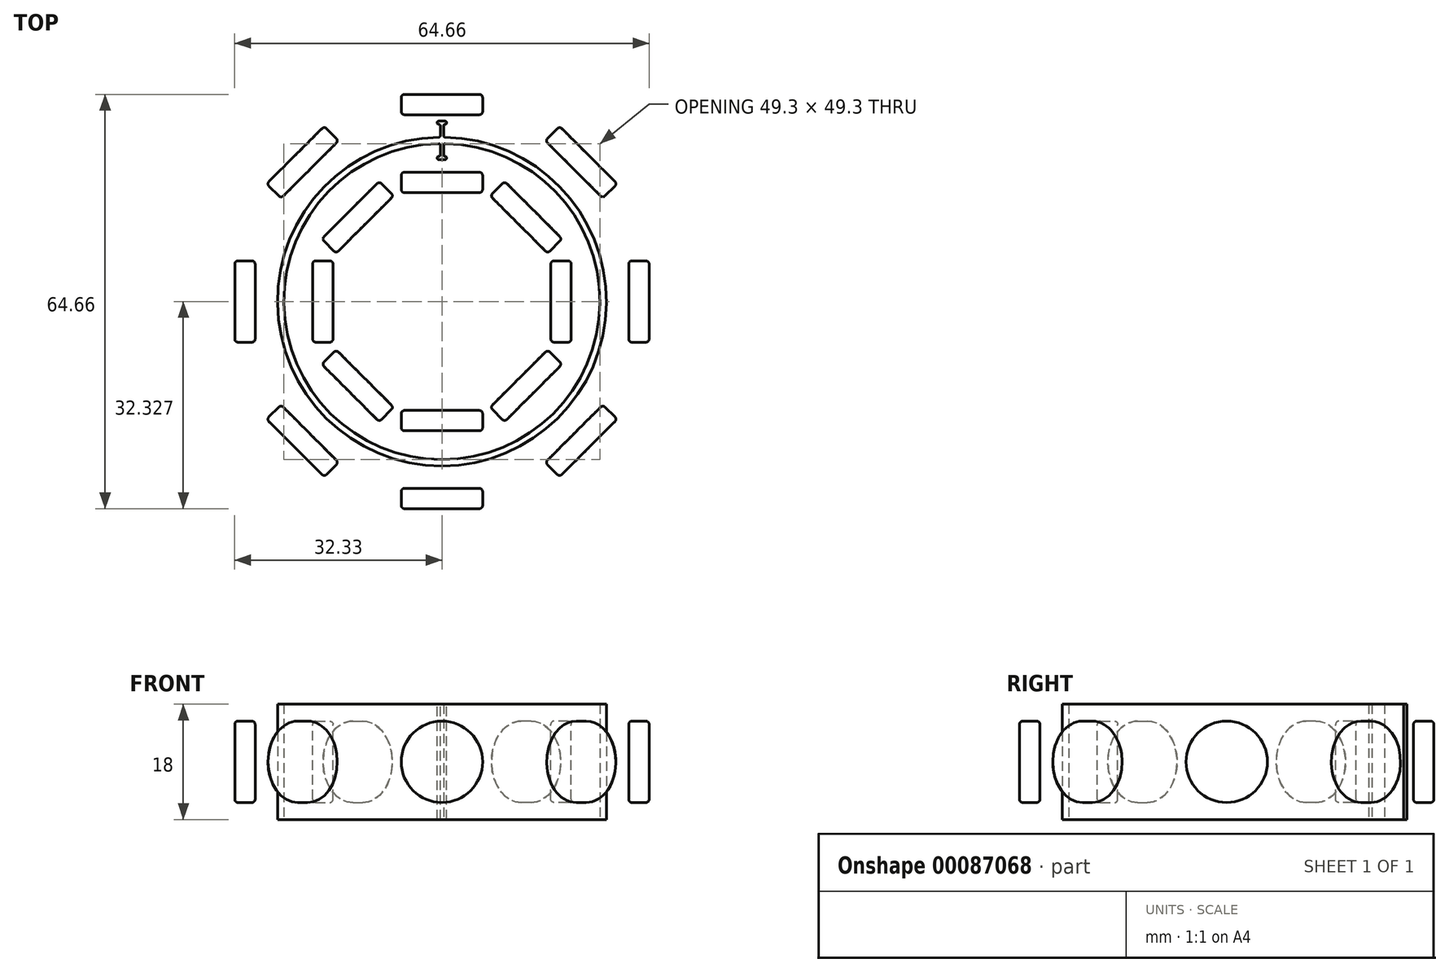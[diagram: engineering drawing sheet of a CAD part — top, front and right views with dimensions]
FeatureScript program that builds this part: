
annotation { "Feature Type Name" : "Feature", "Feature Type Description" : "" }
export const myFeature = defineFeature(function(context is Context, id is Id, definition is map)
    precondition{}
    {
        {
            var Q0;
            Q0=qCreatedBy(makeId("Top.planeOp"),FACE);
            var sketch = newSketch(context, id + "F0", { "sketchPlane" : qUnion([Q0])});
            skLineSegment(sketch, "E0", {"start": v(0, 0) * mm, "end": v(0, 17) * mm, "construction": true});
            skLineSegment(sketch, "E1.bottom", {"start": v(0, 17) * mm, "end": v(6.35, 17) * mm});
            skLineSegment(sketch, "E1.top", {"start": v(0, 20.17) * mm, "end": v(6.35, 20.17) * mm});
            skLineSegment(sketch, "E1.left", {"start": v(0, 17) * mm, "end": v(0, 20.17) * mm});
            skLineSegment(sketch, "E1.right", {"start": v(6.35, 17) * mm, "end": v(6.35, 20.17) * mm});
            skCircle(sketch, "E2", {"center": v(0, 0) * mm, "radius": 24.65 * mm});
            skCircle(sketch, "E3", {"center": v(0, 0) * mm, "radius": 25.65 * mm});
            skCircle(sketch, "E4", {"center": v(0, 0) * mm, "radius": 21.15 * mm, "construction": true});
            skLineSegment(sketch, "E5", {"start": v(0, 24.65) * mm, "end": v(0, 25.65) * mm, "construction": true});
            skLineSegment(sketch, "E6", {"start": v(0, 25.65) * mm, "end": v(0, 28.15) * mm, "construction": true});
            skLineSegment(sketch, "E7", {"start": v(0, 24.65) * mm, "end": v(0, 22.15) * mm, "construction": true});
            skCircle(sketch, "E8", {"center": v(0, 0) * mm, "radius": 29.15 * mm, "construction": true});
            skLineSegment(sketch, "E9", {"start": v(-29.15, 0) * mm, "end": v(-25.65, 0) * mm, "construction": true});
            skLineSegment(sketch, "E10", {"start": v(-25.65, 0) * mm, "end": v(-24.65, 0) * mm, "construction": true});
            skLineSegment(sketch, "E11", {"start": v(-24.65, 0) * mm, "end": v(-21.15, 0) * mm, "construction": true});
            skLineSegment(sketch, "E12.bottom", {"start": v(0, 29.15) * mm, "end": v(6.35, 29.15) * mm});
            skLineSegment(sketch, "E12.top", {"start": v(0, 32.33) * mm, "end": v(6.35, 32.33) * mm});
            skLineSegment(sketch, "E12.left", {"start": v(0, 29.15) * mm, "end": v(0, 32.33) * mm});
            skLineSegment(sketch, "E12.right", {"start": v(6.35, 29.15) * mm, "end": v(6.35, 32.33) * mm});
            skLineSegment(sketch, "E13.bottom", {"start": v(0.25, 28.15) * mm, "end": v(-0.25, 28.15) * mm});
            skLineSegment(sketch, "E13.top", {"start": v(0.25, 22.15) * mm, "end": v(-0.25, 22.15) * mm});
            skLineSegment(sketch, "E13.left", {"start": v(0.25, 28.15) * mm, "end": v(0.25, 22.15) * mm});
            skLineSegment(sketch, "E13.right", {"start": v(-0.25, 28.15) * mm, "end": v(-0.25, 22.15) * mm});
            skPoint(sketch, "E13.middle", {"position": v(0, 25.15) * mm});
            skLineSegment(sketch, "E14.bottom", {"start": v(-0.75, 22.65) * mm, "end": v(0.75, 22.65) * mm});
            skLineSegment(sketch, "E14.top", {"start": v(-0.75, 22.15) * mm, "end": v(0.75, 22.15) * mm});
            skLineSegment(sketch, "E14.left", {"start": v(-0.75, 22.65) * mm, "end": v(-0.75, 22.15) * mm});
            skLineSegment(sketch, "E14.right", {"start": v(0.75, 22.65) * mm, "end": v(0.75, 22.15) * mm});
            skLineSegment(sketch, "E15.bottom", {"start": v(-0.75, 27.65) * mm, "end": v(0.75, 27.65) * mm});
            skLineSegment(sketch, "E15.top", {"start": v(-0.75, 28.15) * mm, "end": v(0.75, 28.15) * mm});
            skLineSegment(sketch, "E15.left", {"start": v(-0.75, 27.65) * mm, "end": v(-0.75, 28.15) * mm});
            skLineSegment(sketch, "E15.right", {"start": v(0.75, 27.65) * mm, "end": v(0.75, 28.15) * mm});
            skSolve(sketch);
        }
        {
            var Q0;
            Q0=makeQuery(id+"F0.imprint","IMPRINT",FACE,{"disambiguationData":[TD([[makeQuery(id+"F0.imprint","IMPRINT",EDGE,{"derivedFrom":sQuery(id+"F0.wireOp",EDGE,"E12.bottom")}),1.0]])]});
            var Q1;
            Q1=makeQuery(id+"F0.imprint","IMPRINT",FACE,{"disambiguationData":[TD([[makeQuery(id+"F0.imprint","IMPRINT",EDGE,{"derivedFrom":sQuery(id+"F0.wireOp",EDGE,"E1.bottom")}),1.0]])]});
            var Q2;
            Q2=sQuery(id+"F0.wireOp",EDGE,"E0");
            revolve(context, id + "F1", {"entities" : qUnion([Q0, Q1]), "axis" : qUnion([Q2]), "revolveType" : RevolveType.FULL});
        }
        {
            var Q0;
            Q0=makeQuery(id+"F1.opRevolve","SWEPT_FACE",FACE,{"disambiguationData":[OSD([sQuery(id+"F0.wireOp",EDGE,"E1.top")])]});
            var Q1;
            Q1=makeQuery(id+"F1.opRevolve","SWEPT_FACE",FACE,{"disambiguationData":[OSD([sQuery(id+"F0.wireOp",EDGE,"E12.top")])]});
            var Q2;
            Q2=makeQuery(id+"F1.opRevolve","SWEPT_FACE",FACE,{"disambiguationData":[OSD([sQuery(id+"F0.wireOp",EDGE,"E12.bottom")])]});
            var Q3;
            Q3=makeQuery(id+"F1.opRevolve","SWEPT_FACE",FACE,{"disambiguationData":[OSD([sQuery(id+"F0.wireOp",EDGE,"E1.bottom")])]});
            fillet(context, id + "F2", {"entities" : qUnion([Q0, Q1, Q2, Q3]), "radius" : .5 * mm, "tangentPropagation" : true, "allowEdgeOverflow" : false});
        }
        {
            var Q0;
            Q0=makeQuery(id+"F1.opRevolve","SWEPT_BODY",BODY,{"disambiguationData":[OSD([sQuery(id+"F0.wireOp",EDGE,"E12.bottom"),sQuery(id+"F0.wireOp",EDGE,"E12.top"),sQuery(id+"F0.wireOp",EDGE,"E12.left"),sQuery(id+"F0.wireOp",EDGE,"E12.right")])]});
            var Q1;
            Q1=makeQuery(id+"F1.opRevolve","SWEPT_BODY",BODY,{"disambiguationData":[OSD([sQuery(id+"F0.wireOp",EDGE,"E1.bottom"),sQuery(id+"F0.wireOp",EDGE,"E1.top"),sQuery(id+"F0.wireOp",EDGE,"E1.left"),sQuery(id+"F0.wireOp",EDGE,"E1.right")])]});
            var Q2;
            Q2=sQuery(id+"F0.wireOp",EDGE,"E3");
            circularPattern(context, id + "F3", {"entities" : qUnion([Q0, Q1]), "axis" : qUnion([Q2]), "angle" : 360 * degree, "instanceCount" : 8, "equalSpace" : true});
        }
        {
            var Q0;
            {var subQ0=sQuery(id+"F0.wireOp",EDGE,"E13.left");var subQ1=sQuery(id+"F0.wireOp",EDGE,"E2");var subQ2=makeQuery(id+"F0.imprint","INTERSECT",VERTEX,{"derivedFrom":[subQ1,subQ0]});Q0=makeQuery(id+"F0.imprint","IMPRINT",FACE,{"disambiguationData":[TD([[makeQuery(id+"F0.imprint","IMPRINT",EDGE,{"disambiguationData":[TD([[subQ2,1.0]])],"derivedFrom":subQ1}),-1.0]])]});}
            var Q1;
            {var subQ0=sQuery(id+"F0.wireOp",EDGE,"E13.left");var subQ1=sQuery(id+"F0.wireOp",EDGE,"E2");var subQ2=makeQuery(id+"F0.imprint","INTERSECT",VERTEX,{"derivedFrom":[subQ1,subQ0]});Q1=makeQuery(id+"F0.imprint","IMPRINT",FACE,{"disambiguationData":[TD([[makeQuery(id+"F0.imprint","IMPRINT",EDGE,{"disambiguationData":[TD([[subQ2,-1.0]])],"derivedFrom":subQ1}),-1.0]])]});}
            extrude(context, id + "F4", {"entities" : qUnion([Q0, Q1]), "depth" : 18 * mm, "symmetric" : true});
        }
        {
            var Q0;
            {var subQ5=sQuery(id+"F0.wireOp",EDGE,"E15.left");Q0=makeQuery(id+"F0.imprint","IMPRINT",FACE,{"disambiguationData":[TD([[makeQuery(id+"F0.imprint","IMPRINT",EDGE,{"derivedFrom":subQ5}),-1.0]])]});}
            var Q1;
            {var subQ0=sQuery(id+"F0.wireOp",EDGE,"E15.top");var subQ1=sQuery(id+"F0.wireOp",EDGE,"E13.left");var subQ2=makeQuery(id+"F0.imprint","INTERSECT",VERTEX,{"derivedFrom":[subQ1,subQ0]});Q1=makeQuery(id+"F0.imprint","IMPRINT",FACE,{"disambiguationData":[TD([[makeQuery(id+"F0.imprint","IMPRINT",EDGE,{"disambiguationData":[TD([[subQ2,-1.0]])],"derivedFrom":subQ1}),-1.0]])]});}
            var Q2;
            {var subQ5=sQuery(id+"F0.wireOp",EDGE,"E15.right");Q2=makeQuery(id+"F0.imprint","IMPRINT",FACE,{"disambiguationData":[TD([[makeQuery(id+"F0.imprint","IMPRINT",EDGE,{"derivedFrom":subQ5}),1.0]])]});}
            var Q3;
            {var subQ0=sQuery(id+"F0.wireOp",EDGE,"E13.left");var subQ1=sQuery(id+"F0.wireOp",EDGE,"E3");var subQ2=makeQuery(id+"F0.imprint","INTERSECT",VERTEX,{"derivedFrom":[subQ1,subQ0]});Q3=makeQuery(id+"F0.imprint","IMPRINT",FACE,{"disambiguationData":[TD([[makeQuery(id+"F0.imprint","IMPRINT",EDGE,{"disambiguationData":[TD([[subQ2,-1.0]])],"derivedFrom":subQ1}),-1.0]])]});}
            var Q4;
            {var subQ0=sQuery(id+"F0.wireOp",EDGE,"E13.left");var subQ1=sQuery(id+"F0.wireOp",EDGE,"E2");var subQ2=makeQuery(id+"F0.imprint","INTERSECT",VERTEX,{"derivedFrom":[subQ1,subQ0]});Q4=makeQuery(id+"F0.imprint","IMPRINT",FACE,{"disambiguationData":[TD([[makeQuery(id+"F0.imprint","IMPRINT",EDGE,{"disambiguationData":[TD([[subQ2,-1.0]])],"derivedFrom":subQ1}),-1.0]])]});}
            var Q5;
            {var subQ0=sQuery(id+"F0.wireOp",EDGE,"E13.left");var subQ1=sQuery(id+"F0.wireOp",EDGE,"E2");var subQ2=makeQuery(id+"F0.imprint","INTERSECT",VERTEX,{"derivedFrom":[subQ1,subQ0]});Q5=makeQuery(id+"F0.imprint","IMPRINT",FACE,{"disambiguationData":[TD([[makeQuery(id+"F0.imprint","IMPRINT",EDGE,{"disambiguationData":[TD([[subQ2,-1.0]])],"derivedFrom":subQ1}),1.0]])]});}
            var Q6;
            {var subQ0=sQuery(id+"F0.wireOp",EDGE,"E14.top");var subQ1=sQuery(id+"F0.wireOp",EDGE,"E13.left");var subQ2=makeQuery(id+"F0.imprint","INTERSECT",VERTEX,{"derivedFrom":[subQ1,subQ0]});Q6=makeQuery(id+"F0.imprint","IMPRINT",FACE,{"disambiguationData":[TD([[makeQuery(id+"F0.imprint","IMPRINT",EDGE,{"disambiguationData":[TD([[subQ2,1.0]])],"derivedFrom":subQ1}),-1.0]])]});}
            var Q7;
            {var subQ5=sQuery(id+"F0.wireOp",EDGE,"E14.left");Q7=makeQuery(id+"F0.imprint","IMPRINT",FACE,{"disambiguationData":[TD([[makeQuery(id+"F0.imprint","IMPRINT",EDGE,{"derivedFrom":subQ5}),1.0]])]});}
            var Q8;
            {var subQ5=sQuery(id+"F0.wireOp",EDGE,"E14.right");Q8=makeQuery(id+"F0.imprint","IMPRINT",FACE,{"disambiguationData":[TD([[makeQuery(id+"F0.imprint","IMPRINT",EDGE,{"derivedFrom":subQ5}),-1.0]])]});}
            extrude(context, id + "F5", {"entities" : qUnion([Q0, Q1, Q2, Q3, Q4, Q5, Q6, Q7, Q8]), "operationType" : NewBodyOperationType.ADD, "depth" : 18 * mm, "symmetric" : true});
        }
        {
            var Q0;
            Q0=makeQuery(id+"F5.opExtrude","SWEPT_EDGE",EDGE,{"disambiguationData":[OSD([sQuery(id+"F0.wireOp",EDGE,"E13.right"),sQuery(id+"F0.wireOp",EDGE,"E15.bottom")])]});
            var Q1;
            Q1=makeQuery(id+"F5.opExtrude","SWEPT_EDGE",EDGE,{"disambiguationData":[OSD([sQuery(id+"F0.wireOp",EDGE,"E15.bottom"),sQuery(id+"F0.wireOp",EDGE,"E15.left")])]});
            var Q2;
            Q2=makeQuery(id+"F5.opExtrude","SWEPT_EDGE",EDGE,{"disambiguationData":[OSD([sQuery(id+"F0.wireOp",EDGE,"E15.top"),sQuery(id+"F0.wireOp",EDGE,"E15.left")])]});
            var Q3;
            Q3=makeQuery(id+"F5.boolean.opBoolean","INTERSECT",EDGE,{"derivedFrom":[makeQuery(id+"F4.opExtrude","SWEPT_FACE",FACE,{"disambiguationData":[OSD([sQuery(id+"F0.wireOp",EDGE,"E3")])]}),makeQuery(id+"F5.opExtrude","SWEPT_FACE",FACE,{"disambiguationData":[OSD([sQuery(id+"F0.wireOp",EDGE,"E13.right")])]})]});
            var Q4;
            Q4=makeQuery(id+"F5.opExtrude","SWEPT_EDGE",EDGE,{"disambiguationData":[OSD([sQuery(id+"F0.wireOp",EDGE,"E13.right"),sQuery(id+"F0.wireOp",EDGE,"E14.bottom")])]});
            var Q5;
            Q5=makeQuery(id+"F5.opExtrude","SWEPT_EDGE",EDGE,{"disambiguationData":[OSD([sQuery(id+"F0.wireOp",EDGE,"E14.bottom"),sQuery(id+"F0.wireOp",EDGE,"E14.left")])]});
            var Q6;
            Q6=makeQuery(id+"F5.opExtrude","SWEPT_EDGE",EDGE,{"disambiguationData":[OSD([sQuery(id+"F0.wireOp",EDGE,"E14.top"),sQuery(id+"F0.wireOp",EDGE,"E14.left")])]});
            var Q7;
            Q7=makeQuery(id+"F5.boolean.opBoolean","INTERSECT",EDGE,{"derivedFrom":[makeQuery(id+"F4.opExtrude","SWEPT_FACE",FACE,{"disambiguationData":[OSD([sQuery(id+"F0.wireOp",EDGE,"E2")])]}),makeQuery(id+"F5.opExtrude","SWEPT_FACE",FACE,{"disambiguationData":[OSD([sQuery(id+"F0.wireOp",EDGE,"E13.right")])]})]});
            var Q8;
            Q8=makeQuery(id+"F5.boolean.opBoolean","INTERSECT",EDGE,{"derivedFrom":[makeQuery(id+"F4.opExtrude","SWEPT_FACE",FACE,{"disambiguationData":[OSD([sQuery(id+"F0.wireOp",EDGE,"E3")])]}),makeQuery(id+"F5.opExtrude","SWEPT_FACE",FACE,{"disambiguationData":[OSD([sQuery(id+"F0.wireOp",EDGE,"E13.left")])]})]});
            var Q9;
            Q9=makeQuery(id+"F5.opExtrude","SWEPT_EDGE",EDGE,{"disambiguationData":[OSD([sQuery(id+"F0.wireOp",EDGE,"E15.bottom"),sQuery(id+"F0.wireOp",EDGE,"E15.right")])]});
            var Q10;
            Q10=makeQuery(id+"F5.opExtrude","SWEPT_EDGE",EDGE,{"disambiguationData":[OSD([sQuery(id+"F0.wireOp",EDGE,"E15.top"),sQuery(id+"F0.wireOp",EDGE,"E15.right")])]});
            var Q11;
            Q11=makeQuery(id+"F5.opExtrude","SWEPT_EDGE",EDGE,{"disambiguationData":[OSD([sQuery(id+"F0.wireOp",EDGE,"E13.left"),sQuery(id+"F0.wireOp",EDGE,"E14.bottom")])]});
            var Q12;
            Q12=makeQuery(id+"F5.opExtrude","SWEPT_EDGE",EDGE,{"disambiguationData":[OSD([sQuery(id+"F0.wireOp",EDGE,"E14.bottom"),sQuery(id+"F0.wireOp",EDGE,"E14.right")])]});
            var Q13;
            Q13=makeQuery(id+"F5.opExtrude","SWEPT_EDGE",EDGE,{"disambiguationData":[OSD([sQuery(id+"F0.wireOp",EDGE,"E14.top"),sQuery(id+"F0.wireOp",EDGE,"E14.right")])]});
            var Q14;
            Q14=makeQuery(id+"F5.boolean.opBoolean","INTERSECT",EDGE,{"derivedFrom":[makeQuery(id+"F4.opExtrude","SWEPT_FACE",FACE,{"disambiguationData":[OSD([sQuery(id+"F0.wireOp",EDGE,"E2")])]}),makeQuery(id+"F5.opExtrude","SWEPT_FACE",FACE,{"disambiguationData":[OSD([sQuery(id+"F0.wireOp",EDGE,"E13.left")])]})]});
            var Q15;
            Q15=makeQuery(id+"F5.opExtrude","SWEPT_EDGE",EDGE,{"disambiguationData":[OSD([sQuery(id+"F0.wireOp",EDGE,"E13.left"),sQuery(id+"F0.wireOp",EDGE,"E15.bottom")])]});
            fillet(context, id + "F6", {"entities" : qUnion([Q0, Q1, Q2, Q3, Q4, Q5, Q6, Q7, Q8, Q9, Q10, Q11, Q12, Q13, Q14, Q15]), "radius" : .25 * mm, "tangentPropagation" : true, "allowEdgeOverflow" : false});
        }
    });
